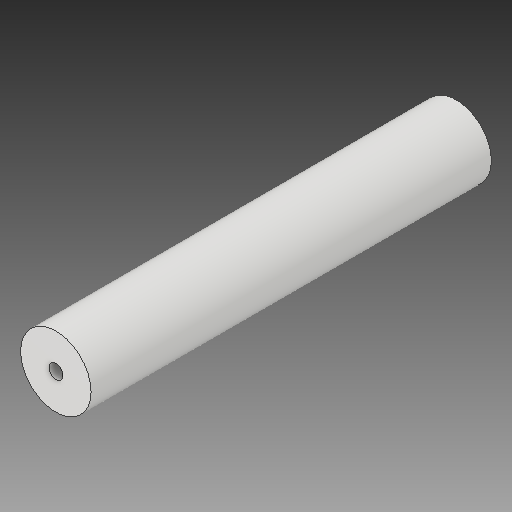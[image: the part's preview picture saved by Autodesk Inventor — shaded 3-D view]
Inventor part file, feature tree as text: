
AUTODESK INVENTOR PART (.ipt)
format: ipt  version: 2019 (Build 230136000, 136)  size: 101,376 bytes
history: native  units: in
note: dims shown in document units (in); Inventor stores cm internally (conversion verified against a paired STEP export)
features: extrude x3, sketch x3
ambient origin geometry x8: Origin, YZ Plane, XZ Plane, XY Plane, X Axis, Y Axis, Z Axis, Center Point
bodies: Solid1 (feature_tree)
feature tree (6):
  extrude  "Extrusion1"  Depth=5.5906in TaperAngle=0.0deg
  extrude  "Extrusion2"  Depth=0.4724in TaperAngle=0.0deg
  extrude  "Extrusion3"  Depth=0.9843in TaperAngle=0.0deg
  sketch  "Sketch1"  dims[d0=0.9843in d1=5.5906in d2=0.0in]
  sketch  "Sketch2"  dims[d3=0.1969in d4=0.4724in d5=0.0in]
  sketch  "Sketch3"  dims[d6=0.1969in d7=0.9843in d8=0.0in]
